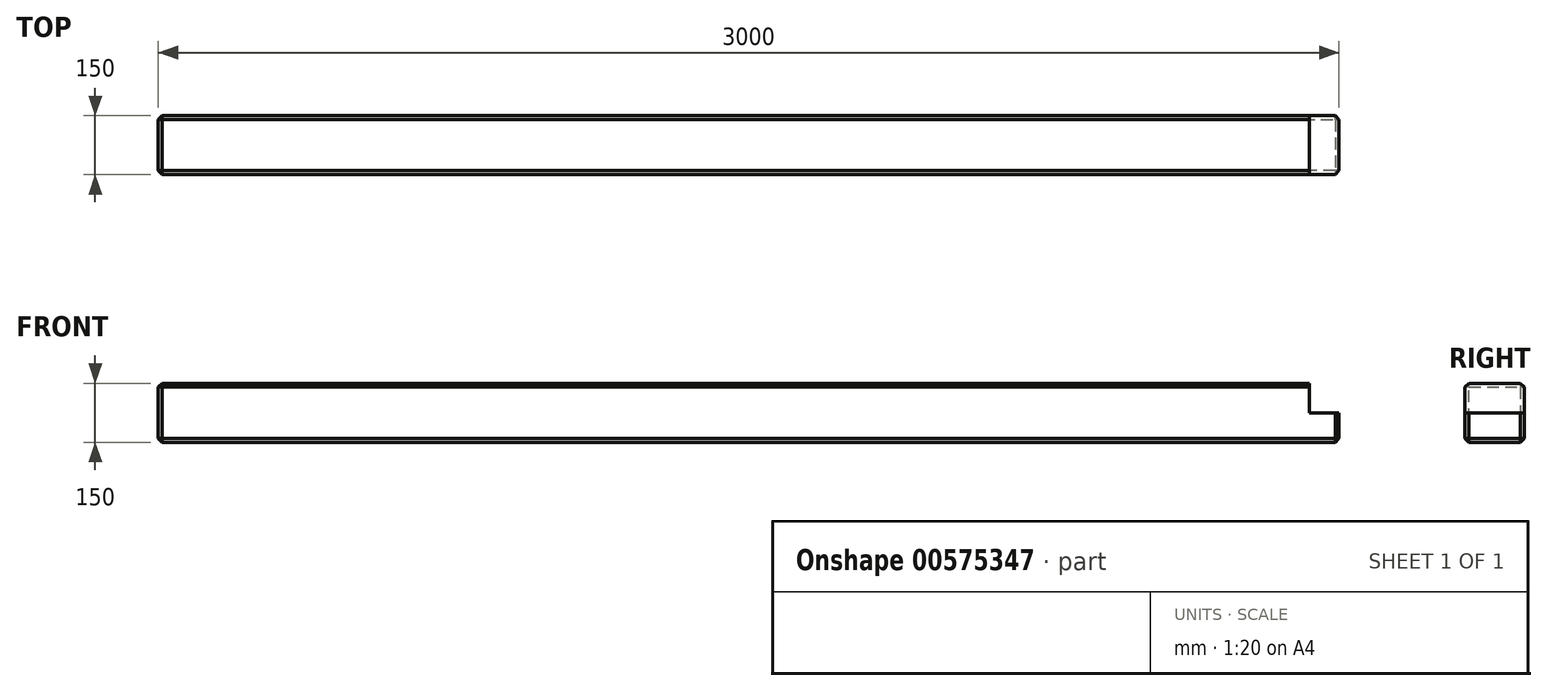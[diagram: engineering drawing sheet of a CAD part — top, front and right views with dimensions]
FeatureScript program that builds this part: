
annotation { "Feature Type Name" : "Feature", "Feature Type Description" : "" }
export const myFeature = defineFeature(function(context is Context, id is Id, definition is map)
    precondition{}
    {
        {
            var Q0;
            Q0=qCreatedBy(makeId("Top.planeOp"),FACE);
            var sketch = newSketch(context, id + "F0", { "sketchPlane" : qUnion([Q0])});
            skLineSegment(sketch, "E0.bottom", {"start": v(-1500, -75) * mm, "end": v(1500, -75) * mm});
            skLineSegment(sketch, "E0.top", {"start": v(-1500, 75) * mm, "end": v(1500, 75) * mm});
            skLineSegment(sketch, "E0.left", {"start": v(-1500, -75) * mm, "end": v(-1500, 75) * mm});
            skLineSegment(sketch, "E0.right", {"start": v(1500, -75) * mm, "end": v(1500, 75) * mm});
            skPoint(sketch, "E0.middle", {"position": v(0, 0) * mm});
            skSolve(sketch);
        }
        {
            var Q0;
            Q0=makeQuery(id+"F0.imprint","IMPRINT",FACE,{"disambiguationData":[TD([[makeQuery(id+"F0.imprint","IMPRINT",EDGE,{"derivedFrom":sQuery(id+"F0.wireOp",EDGE,"E0.bottom")}),1.0]])]});
            extrude(context, id + "F1", {"entities" : qUnion([Q0]), "depth" : 150 * mm});
        }
        {
            var Q0;
            Q0=makeQuery(id+"F1.opExtrude","CAP_FACE",FACE,{"disambiguationData":[OSD([sQuery(id+"F0.wireOp",EDGE,"E0.bottom"),sQuery(id+"F0.wireOp",EDGE,"E0.top"),sQuery(id+"F0.wireOp",EDGE,"E0.left"),sQuery(id+"F0.wireOp",EDGE,"E0.right")])],"isStart":false});
            var Q1;
            Q1=makeQuery(id+"F1.opExtrude","SWEPT_FACE",FACE,{"disambiguationData":[OSD([sQuery(id+"F0.wireOp",EDGE,"E0.bottom")])]});
            var Q2;
            Q2=makeQuery(id+"F1.opExtrude","CAP_FACE",FACE,{"disambiguationData":[OSD([sQuery(id+"F0.wireOp",EDGE,"E0.bottom"),sQuery(id+"F0.wireOp",EDGE,"E0.top"),sQuery(id+"F0.wireOp",EDGE,"E0.left"),sQuery(id+"F0.wireOp",EDGE,"E0.right")])],"isStart":true});
            var Q3;
            Q3=makeQuery(id+"F1.opExtrude","SWEPT_FACE",FACE,{"disambiguationData":[OSD([sQuery(id+"F0.wireOp",EDGE,"E0.top")])]});
            chamfer(context, id + "F2", {"entities" : qUnion([Q0, Q1, Q2, Q3]), "width" : 10 * mm, "tangentPropagation" : true});
        }
        {
            var Q0;
            Q0=makeQuery(id+"F1.opExtrude","SWEPT_FACE",FACE,{"disambiguationData":[OSD([sQuery(id+"F0.wireOp",EDGE,"E0.bottom")])]});
            var sketch = newSketch(context, id + "F3", { "sketchPlane" : qUnion([Q0])});
            skPoint(sketch, "E1", {"position": v(1425, 75) * mm});
            skLineSegment(sketch, "E2.bottom", {"start": v(1425, 75) * mm, "end": v(1500, 75) * mm});
            skLineSegment(sketch, "E2.top", {"start": v(1425, 150) * mm, "end": v(1500, 150) * mm});
            skLineSegment(sketch, "E2.left", {"start": v(1425, 75) * mm, "end": v(1425, 150) * mm});
            skLineSegment(sketch, "E2.right", {"start": v(1500, 75) * mm, "end": v(1500, 150) * mm});
            skSolve(sketch);
        }
        {
            var Q0;
            {var subQ0=sQuery(id+"F3.wireOp",EDGE,"E2.left");var subQ1=sQuery(id+"F3.wireOp",EDGE,"E2.bottom");var subQ2=makeQuery(id+"F3.imprint","INTERSECT",VERTEX,{"derivedFrom":[subQ1,subQ0]});Q0=makeQuery(id+"F3.imprint","IMPRINT",FACE,{"disambiguationData":[TD([[makeQuery(id+"F3.imprint","IMPRINT",EDGE,{"disambiguationData":[TD([[subQ2,-1.0]])],"derivedFrom":subQ0}),-1.0]])]});}
            var Q1;
            {var subQ1=sQuery(id+"F3.wireOp",EDGE,"E2.top");Q1=makeQuery(id+"F3.imprint","IMPRINT",FACE,{"disambiguationData":[TD([[makeQuery(id+"F3.imprint","IMPRINT",EDGE,{"derivedFrom":subQ1}),-1.0]])]});}
            extrude(context, id + "F4", {"entities" : qUnion([Q0, Q1]), "operationType" : NewBodyOperationType.REMOVE, "endBound" : BoundingType.THROUGH_ALL, "oppositeDirection" : true, "depth" : 25 * mm});
        }
    });
